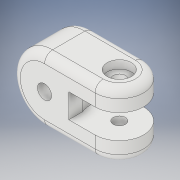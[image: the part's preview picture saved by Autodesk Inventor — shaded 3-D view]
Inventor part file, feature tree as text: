
AUTODESK INVENTOR PART (.ipt)
format: ipt  version: 2017 SP1 (Build 210196100, 196)  size: 200,704 bytes
history: native  units: in
note: dims shown in document units (in); Inventor stores cm internally (conversion verified against a paired STEP export)
features: extrude x5, sketch x5, fillet x1, projected_geometry x1
ambient origin geometry x8: Origin, YZ Plane, XZ Plane, XY Plane, X Axis, Y Axis, Z Axis, Center Point
bodies: Solid1 (feature_tree)
feature tree (12):
  extrude  "Extrusion1"  Depth=0.6299in
  extrude  "Extrusion2"  Depth=0.4724in TaperAngle=0.0deg
  extrude  "Extrusion3"  Depth=0.4724in
  extrude  "Extrusion4"  Depth=0.1969in TaperAngle=0.0deg
  extrude  "Extrusion5"  Depth=0.2362in
  fillet  "Fillet1"  Radius=0.0787in
  sketch  "Sketch2"  dims[d0=0.1378in d1=0.6299in]
  sketch  "Sketch3"  dims[d2=0.2362in d3=0.4724in d4=0.0in]
  sketch  "Sketch4"  dims[d5=0.4724in d6=0.4921in]
  projected_geometry  "Projected Loop1"
  sketch  "Sketch6"  dims[d7=0.1181in d8=0.1969in d9=0.0in]
  sketch  "Sketch7"  dims[d10=0.1969in d11=0.0in d13=0.2362in d14=0.0787in d15=0.0in d16=0.5512in d17=0.2362in d18=0.0in d19=0.0787in]
